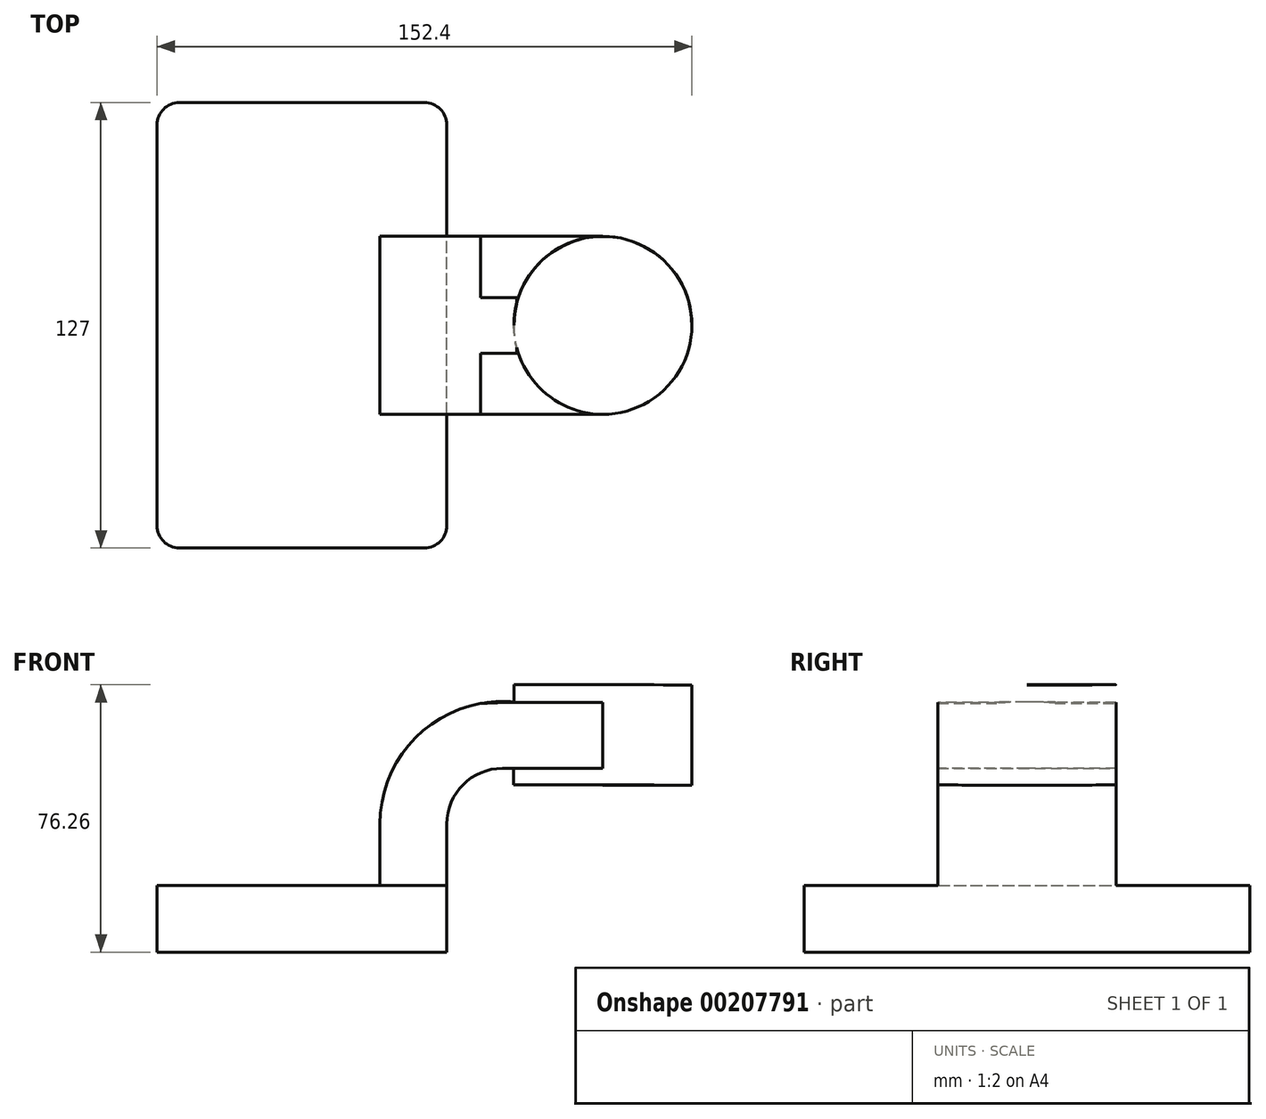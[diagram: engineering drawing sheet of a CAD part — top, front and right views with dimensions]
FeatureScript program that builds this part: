
annotation { "Feature Type Name" : "Feature", "Feature Type Description" : "" }
export const myFeature = defineFeature(function(context is Context, id is Id, definition is map)
    precondition{}
    {
        {
            var Q0;
            Q0=qCreatedBy(makeId("Front.planeOp"),FACE);
            var sketch = newSketch(context, id + "F0", { "sketchPlane" : qUnion([Q0])});
            skLineSegment(sketch, "E0.bottom", {"start": v(-41.28, 9.52) * mm, "end": v(41.28, 9.53) * mm});
            skLineSegment(sketch, "E0.top", {"start": v(-41.28, -9.53) * mm, "end": v(41.28, -9.53) * mm});
            skLineSegment(sketch, "E0.left", {"start": v(-41.28, 9.52) * mm, "end": v(-41.27, -9.53) * mm});
            skLineSegment(sketch, "E0.right", {"start": v(41.28, 9.53) * mm, "end": v(41.28, -9.52) * mm});
            skPoint(sketch, "E0.middle", {"position": v(0, 0) * mm});
            skPoint(sketch, "E1.middle", {"position": v(85.72, 52.39) * mm});
            skLineSegment(sketch, "E2", {"start": v(41.27, 9.53) * mm, "end": v(41.27, 27) * mm});
            skArc(sketch, "E3", {"start": v(41.27, 27) * mm, "mid": v(45.92, 38.23) * mm, "end": v(57.15, 42.88) * mm});
            skArc(sketch, "E4.1", {"start": v(22.22, 27) * mm, "mid": v(33.92, 53.08) * mm, "end": v(61.17, 61.7) * mm});
            skLineSegment(sketch, "E4.2", {"start": v(22.22, 9.53) * mm, "end": v(22.22, 27) * mm});
            skFitSpline(sketch, "E5", {"points": [v(-41.28, 9.52) * mm, v(61.17, 61.7) * mm], "startDerivative": vector(-1.35, 104.77) * mm, "endDerivative": vector(122.25, -0.13) * mm});
            skLineSegment(sketch, "E6", {"start": v(57.15, 42.88) * mm, "end": v(85.73, 42.88) * mm});
            skLineSegment(sketch, "E7", {"start": v(61.17, 61.7) * mm, "end": v(85.75, 61.7) * mm});
            skLineSegment(sketch, "E8.bottom", {"start": v(60.33, 66.68) * mm, "end": v(111.13, 66.68) * mm});
            skLineSegment(sketch, "E8.top", {"start": v(60.33, 38.1) * mm, "end": v(111.13, 38.1) * mm});
            skLineSegment(sketch, "E8.left", {"start": v(60.33, 66.68) * mm, "end": v(60.33, 38.1) * mm});
            skLineSegment(sketch, "E8.right", {"start": v(111.13, 66.68) * mm, "end": v(111.13, 38.1) * mm});
            skLineSegment(sketch, "E9", {"start": v(85.73, 38.1) * mm, "end": v(85.75, 66.68) * mm});
            skSolve(sketch);
        }
        {
            var Q0;
            Q0=makeQuery(id+"F0.imprint","IMPRINT",FACE,{"disambiguationData":[TD([[makeQuery(id+"F0.imprint","IMPRINT",EDGE,{"derivedFrom":sQuery(id+"F0.wireOp",EDGE,"E0.top")}),1.0]])]});
            extrude(context, id + "F1", {"entities" : qUnion([Q0]), "endBound" : BoundingType.SYMMETRIC, "depth" : 127 * mm});
        }
        {
            var Q0;
            {var subQ1=sQuery(id+"F0.wireOp",EDGE,"E2");Q0=makeQuery(id+"F0.imprint","IMPRINT",FACE,{"disambiguationData":[TD([[makeQuery(id+"F0.imprint","IMPRINT",EDGE,{"derivedFrom":subQ1}),1.0]])]});}
            var Q1;
            {var subQ1=sQuery(id+"F0.wireOp",EDGE,"E6");var subQ7=sQuery(id+"F0.wireOp",EDGE,"E9");var subQ9=makeQuery(id+"F0.imprint","INTERSECT",VERTEX,{"derivedFrom":[subQ1,subQ7]});Q1=makeQuery(id+"F0.imprint","IMPRINT",FACE,{"disambiguationData":[TD([[makeQuery(id+"F0.imprint","IMPRINT",EDGE,{"disambiguationData":[TD([[subQ9,1.0]])],"derivedFrom":subQ1}),1.0]])]});}
            extrude(context, id + "F2", {"entities" : qUnion([Q0, Q1]), "operationType" : NewBodyOperationType.ADD, "endBound" : BoundingType.SYMMETRIC, "depth" : 50.8 * mm});
        }
        {
            var Q0;
            Q0=makeQuery(id+"F0.imprint","IMPRINT",FACE,{"disambiguationData":[TD([[makeQuery(id+"F0.imprint","IMPRINT",EDGE,{"derivedFrom":sQuery(id+"F0.wireOp",EDGE,"E4.1")}),1.0]])]});
            extrude(context, id + "F3", {"entities" : qUnion([Q0]), "operationType" : NewBodyOperationType.ADD, "endBound" : BoundingType.SYMMETRIC, "depth" : 15.88 * mm});
        }
        {
            var Q0;
            {var subQ4=sQuery(id+"F0.wireOp",EDGE,"E8.right");Q0=makeQuery(id+"F0.imprint","IMPRINT",FACE,{"disambiguationData":[TD([[makeQuery(id+"F0.imprint","IMPRINT",EDGE,{"derivedFrom":subQ4}),-1.0]])]});}
            var Q1;
            Q1=sQuery(id+"F0.wireOp",EDGE,"E9");
            revolve(context, id + "F4", {"operationType" : NewBodyOperationType.ADD, "entities" : qUnion([Q0]), "axis" : qUnion([Q1]), "revolveType" : RevolveType.FULL});
        }
        {
            var Q0;
            Q0=makeQuery(id+"F1.opExtrude","CAP_EDGE",EDGE,{"disambiguationData":[OSD([sQuery(id+"F0.wireOp",EDGE,"E0.left")])],"isStart":false});
            var Q1;
            Q1=makeQuery(id+"F1.opExtrude","CAP_EDGE",EDGE,{"disambiguationData":[OSD([sQuery(id+"F0.wireOp",EDGE,"E0.right")])],"isStart":false});
            var Q2;
            Q2=makeQuery(id+"F1.opExtrude","CAP_EDGE",EDGE,{"disambiguationData":[OSD([sQuery(id+"F0.wireOp",EDGE,"E0.right")])],"isStart":true});
            var Q3;
            Q3=makeQuery(id+"F1.opExtrude","CAP_EDGE",EDGE,{"disambiguationData":[OSD([sQuery(id+"F0.wireOp",EDGE,"E0.left")])],"isStart":true});
            fillet(context, id + "F5", {"entities" : qUnion([Q0, Q1, Q2, Q3]), "radius" : 6.35 * mm, "tangentPropagation" : true, "allowEdgeOverflow" : false});
        }
    });
